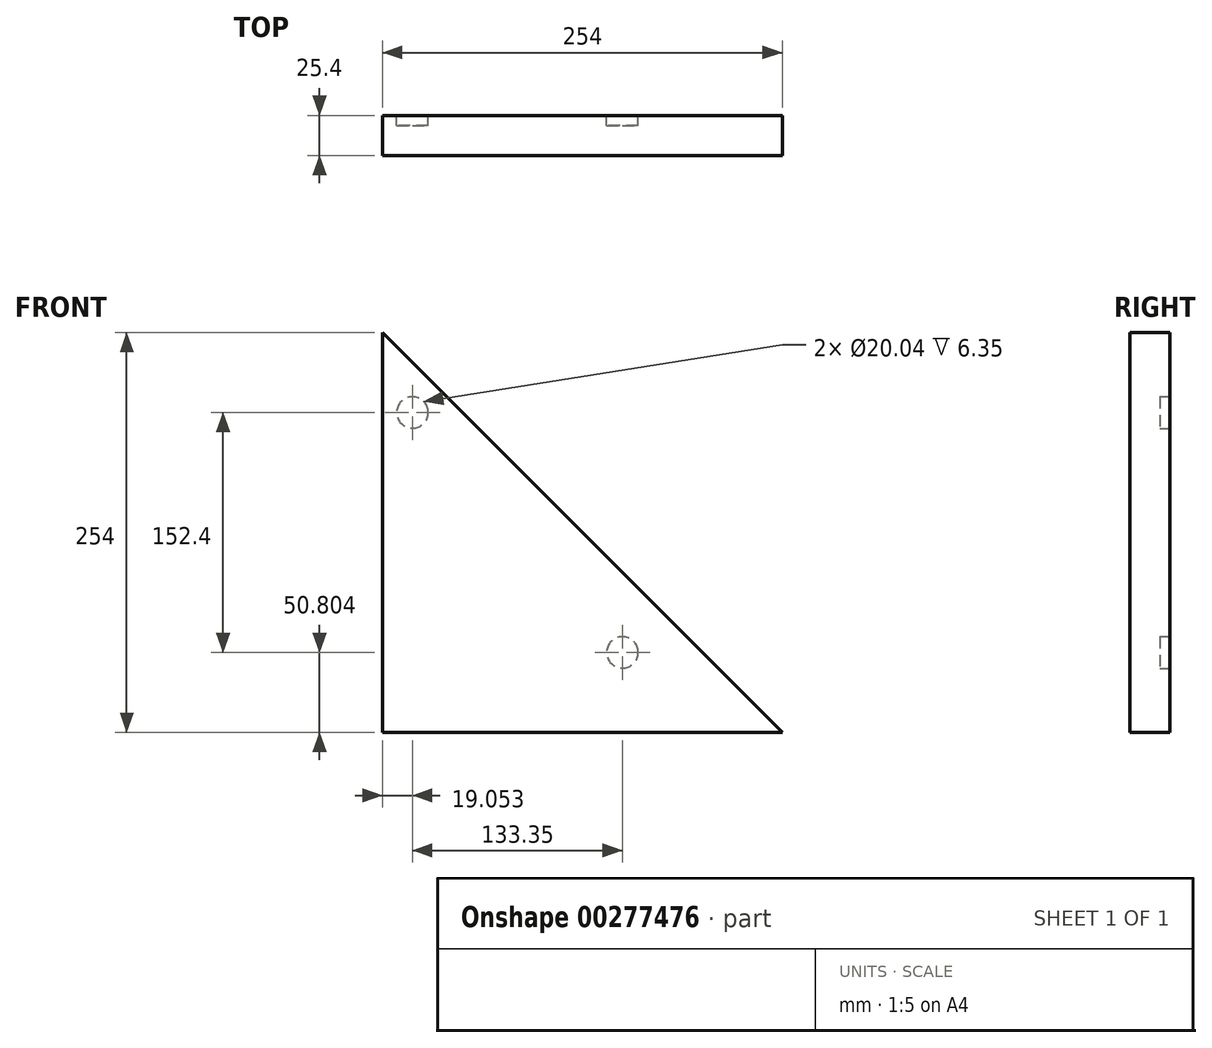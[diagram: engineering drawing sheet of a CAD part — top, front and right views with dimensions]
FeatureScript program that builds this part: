
annotation { "Feature Type Name" : "Feature", "Feature Type Description" : "" }
export const myFeature = defineFeature(function(context is Context, id is Id, definition is map)
    precondition{}
    {
        {
            var Q0;
            Q0=qCreatedBy(makeId("Front.planeOp"),FACE);
            var sketch = newSketch(context, id + "F0", { "sketchPlane" : qUnion([Q0])});
            skLineSegment(sketch, "E0.bottom", {"start": v(-41.24, 85.5) * mm, "end": v(212.76, 85.5) * mm});
            skLineSegment(sketch, "E0.top", {"start": v(-41.24, -168.5) * mm, "end": v(212.76, -168.5) * mm});
            skLineSegment(sketch, "E0.left", {"start": v(-41.24, 85.5) * mm, "end": v(-41.24, -168.5) * mm});
            skLineSegment(sketch, "E0.right", {"start": v(212.76, 85.5) * mm, "end": v(212.76, -168.5) * mm});
            skLineSegment(sketch, "E1", {"start": v(-41.24, 85.5) * mm, "end": v(212.76, -168.5) * mm});
            skSolve(sketch);
        }
        {
            var Q0;
            Q0=makeQuery(id+"F0.imprint","IMPRINT",FACE,{"disambiguationData":[TD([[makeQuery(id+"F0.imprint","IMPRINT",EDGE,{"derivedFrom":sQuery(id+"F0.wireOp",EDGE,"E0.top")}),1.0]])]});
            extrude(context, id + "F1", {"entities" : qUnion([Q0]), "depth" : 25.4 * mm});
        }
        {
            var Q0;
            Q0=makeQuery(id+"F1.opExtrude","CAP_FACE",FACE,{"disambiguationData":[OSD([sQuery(id+"F0.wireOp",EDGE,"E0.top"),sQuery(id+"F0.wireOp",EDGE,"E0.left"),sQuery(id+"F0.wireOp",EDGE,"E1")])],"isStart":true});
            var sketch = newSketch(context, id + "F2", { "sketchPlane" : qUnion([Q0])});
            skCircle(sketch, "E2", {"center": v(22.19, 34.7) * mm, "radius": 10.02 * mm});
            skCircle(sketch, "E3", {"center": v(-111.16, -117.7) * mm, "radius": 10.02 * mm});
            skSolve(sketch);
        }
        {
            var Q0;
            Q0 = qSketchRegion(id + "F2", true);
            extrude(context, id + "F3", {"entities" : qUnion([Q0]), "operationType" : NewBodyOperationType.REMOVE, "oppositeDirection" : true, "depth" : 6.35 * mm});
        }
    });
